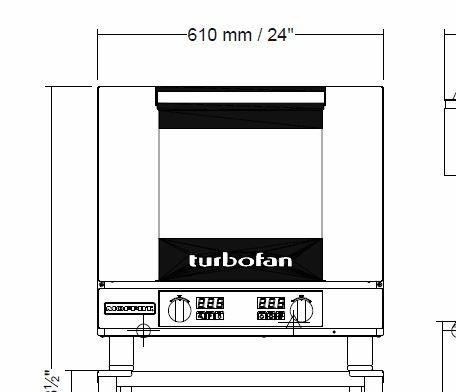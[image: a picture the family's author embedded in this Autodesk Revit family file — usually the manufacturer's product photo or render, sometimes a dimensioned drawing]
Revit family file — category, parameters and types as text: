
# Revit family: QF_MOFFAT_E30M3-2_UK
name_source: partatom
category: Specialty Equipment
revit_build: Autodesk Revit 2014 (Build: 20130308_1515(x64)
units: mm (PartAtom-declared; Revit-internal decimal feet)

## types (1)
- QF_MOFFAT_E30M3-2_UK
    Apparent Power = 2185 VA
    Conn Conduit = Yes
    Depth = 666 mm  [stored 2.18504 ft]
    Description = GN 1/1 MANUAL / ELECTRIC CONVECTION OVENS DOUBLE STACKED ON A STAINLESS STEEL BASE STAND
    Elec Conn Connection Height = 0 mm  [stored 0 ft]
    Elec Conn RI Height = 0 mm  [stored 0 ft]
    Electrical Remarks = 230-240V, 50Hz, 1P+N+E, 2.3kW, 9.5A
    Exhaust RI Height = 0 mm  [stored 0 ft]
    Exhaust Static Press = 0.00 in-wg
    Exhaust Vent Depth = 0 mm  [stored 0 ft]
    Exhaust Vent Diameter = 0 mm  [stored 0 ft]
    Exhaust Vent Width = 0 mm  [stored 0 ft]
    Exhaust Volume = 0 CFM
    FL Amps = 10 A
    Foodservice Equipment Identifier = Yes
    Height = 1636 mm  [stored 5.36745 ft]
    Height of Stand = 454 mm  [stored 1.4895 ft]
    Identify Quantity as Lot = Yes
    Length = 810 mm  [stored 2.65748 ft]
    Manufacturer = MOFFAT
    Max Overcurrent Protection = 0 A
    Min Ckt Ampacity = 0 A
    Model = E30M3-2
    Number of Poles = 1
    Phase = 1
    Volts = 230 V
    Watts = 2300 W
    Weight in Pounds = 0

note: [stored X ft] marks values corroborated as IEEE doubles in the binary element streams (Revit-internal decimal feet)

## geometry (parser evidence)
native form markers: Blend x14, Sweep x8
no freeform markers — native parametric forms only
